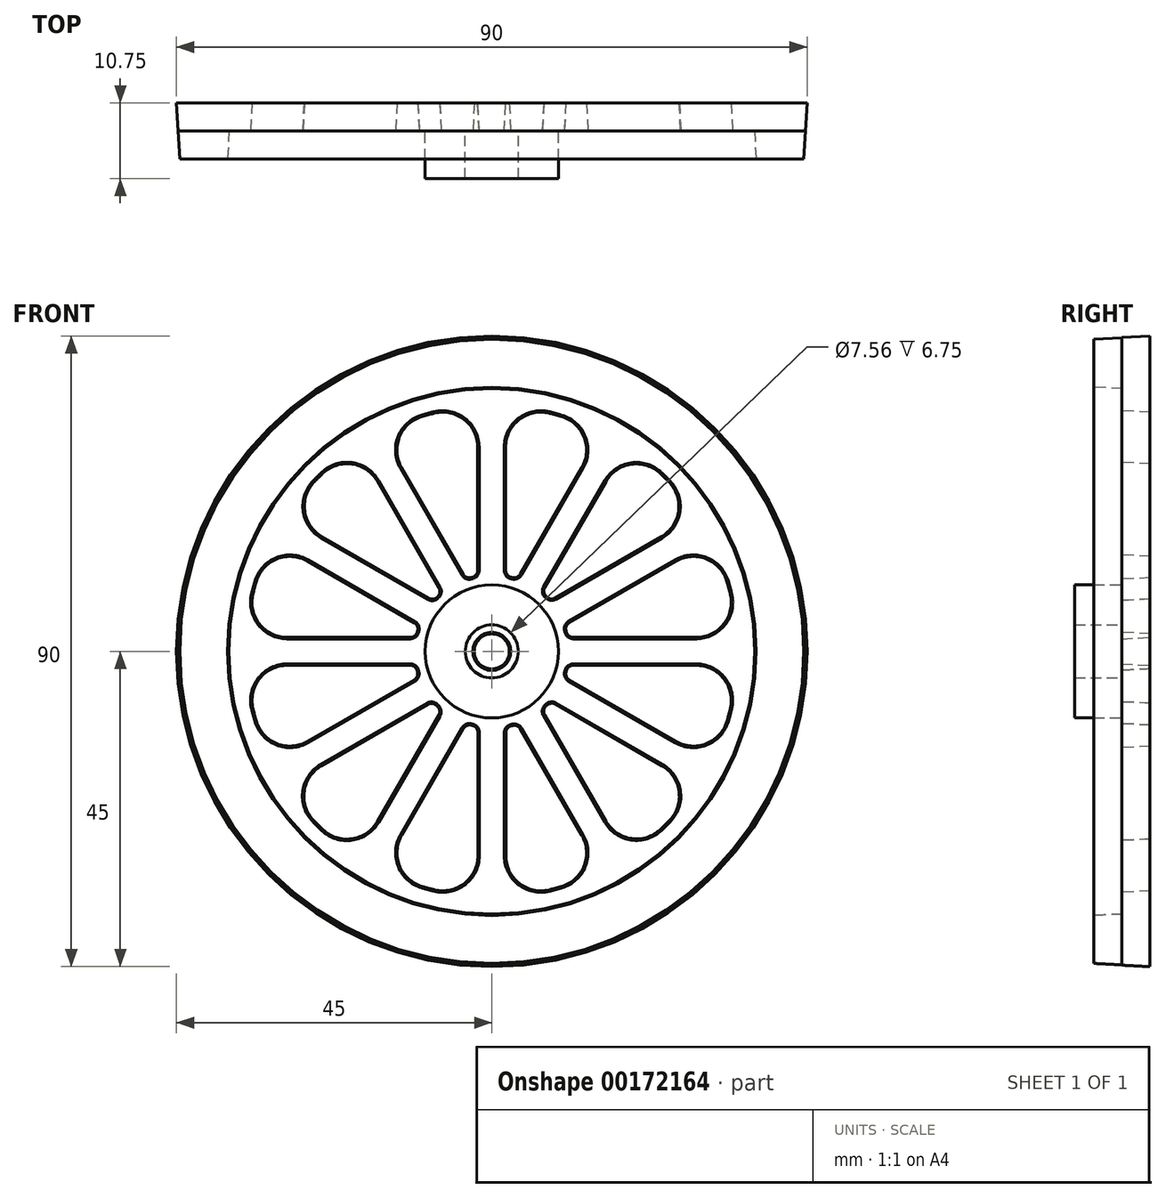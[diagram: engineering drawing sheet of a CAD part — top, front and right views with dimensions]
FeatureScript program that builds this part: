
annotation { "Feature Type Name" : "Feature", "Feature Type Description" : "" }
export const myFeature = defineFeature(function(context is Context, id is Id, definition is map)
    precondition{}
    {
        {
            var Q0;
            Q0=qCreatedBy(makeId("Front.planeOp"),FACE);
            var sketch = newSketch(context, id + "F0", { "sketchPlane" : qUnion([Q0])});
            skCircle(sketch, "E0", {"center": v(0, 0) * mm, "radius": 2.5 * mm});
            skLineSegment(sketch, "E1", {"start": v(1.99, 29.14) * mm, "end": v(1.99, 11.55) * mm});
            skLineSegment(sketch, "E2", {"start": v(-2.01, 11.55) * mm, "end": v(-2.01, 29.14) * mm});
            skLineSegment(sketch, "E3", {"start": v(4.04, 11) * mm, "end": v(12.85, 26.23) * mm});
            skLineSegment(sketch, "E4", {"start": v(7.56, 9.11) * mm, "end": v(16.3, 24.26) * mm});
            skLineSegment(sketch, "E5", {"start": v(9.04, 7.62) * mm, "end": v(24.2, 16.36) * mm});
            skLineSegment(sketch, "E6", {"start": v(11.06, 4.1) * mm, "end": v(26.26, 12.88) * mm});
            skLineSegment(sketch, "E7", {"start": v(11.62, 2) * mm, "end": v(29.18, 2) * mm});
            skLineSegment(sketch, "E8", {"start": v(11.62, -2) * mm, "end": v(29.17, -2) * mm});
            skLineSegment(sketch, "E9", {"start": v(4.07, -11.06) * mm, "end": v(12.85, -26.27) * mm});
            skLineSegment(sketch, "E10", {"start": v(2, -11.62) * mm, "end": v(2, -29.18) * mm});
            skLineSegment(sketch, "E11", {"start": v(-1.99, -11.56) * mm, "end": v(-1.99, -29.17) * mm});
            skLineSegment(sketch, "E12", {"start": v(-4.05, -11.01) * mm, "end": v(-12.85, -26.26) * mm});
            skLineSegment(sketch, "E13", {"start": v(-7.57, -9.1) * mm, "end": v(-16.34, -24.3) * mm});
            skLineSegment(sketch, "E14", {"start": v(-9.12, -7.56) * mm, "end": v(-24.31, -16.33) * mm});
            skLineSegment(sketch, "E15", {"start": v(-11.07, -4.06) * mm, "end": v(-26.3, -12.85) * mm});
            skLineSegment(sketch, "E16", {"start": v(-11.06, 4.08) * mm, "end": v(-26.3, 12.88) * mm});
            skLineSegment(sketch, "E17", {"start": v(-9.01, 7.58) * mm, "end": v(-24.25, 16.38) * mm});
            skLineSegment(sketch, "E18", {"start": v(-7.54, 9.05) * mm, "end": v(-16.34, 24.29) * mm});
            skLineSegment(sketch, "E19", {"start": v(-4.08, 11) * mm, "end": v(-12.87, 26.23) * mm});
            skLineSegment(sketch, "E20", {"start": v(26.27, -12.86) * mm, "end": v(11.07, -4.08) * mm});
            skLineSegment(sketch, "E21", {"start": v(7.54, -9.07) * mm, "end": v(16.31, -24.27) * mm});
            skLineSegment(sketch, "E22", {"start": v(9.06, -7.54) * mm, "end": v(24.27, -16.32) * mm});
            skLineSegment(sketch, "E23", {"start": v(-11.63, -2) * mm, "end": v(-29.21, -2) * mm});
            skLineSegment(sketch, "E24", {"start": v(-11.62, 2) * mm, "end": v(-29.22, 2) * mm});
            skArc(sketch, "E25", {"start": v(25.4, -24.1) * mm, "mid": v(24.75, -24.75) * mm, "end": v(24.09, -25.4) * mm});
            skArc(sketch, "E26", {"start": v(9.94, -33.57) * mm, "mid": v(9.06, -33.81) * mm, "end": v(8.17, -34.04) * mm});
            skArc(sketch, "E27", {"start": v(-8.15, -34.03) * mm, "mid": v(-9.05, -33.8) * mm, "end": v(-9.94, -33.56) * mm});
            skArc(sketch, "E28", {"start": v(-24.11, -25.43) * mm, "mid": v(-24.79, -24.77) * mm, "end": v(-25.45, -24.1) * mm});
            skArc(sketch, "E29", {"start": v(-33.6, -9.94) * mm, "mid": v(-33.85, -9.06) * mm, "end": v(-34.08, -8.17) * mm});
            skArc(sketch, "E30", {"start": v(-34.08, 8.16) * mm, "mid": v(-33.85, 9.07) * mm, "end": v(-33.6, 9.97) * mm});
            skArc(sketch, "E31", {"start": v(33.56, -9.95) * mm, "mid": v(33.81, -9.06) * mm, "end": v(34.04, -8.17) * mm});
            skArc(sketch, "E32", {"start": v(34.04, 8.17) * mm, "mid": v(33.81, 9.07) * mm, "end": v(33.56, 9.97) * mm});
            skArc(sketch, "E33", {"start": v(25.31, 24.15) * mm, "mid": v(24.7, 24.77) * mm, "end": v(24.07, 25.38) * mm});
            skArc(sketch, "E34", {"start": v(9.94, 33.53) * mm, "mid": v(9.05, 33.78) * mm, "end": v(8.15, 34) * mm});
            skArc(sketch, "E35", {"start": v(-8.18, 34) * mm, "mid": v(-9.07, 33.78) * mm, "end": v(-9.96, 33.53) * mm});
            skArc(sketch, "E36", {"start": v(-24.1, 25.42) * mm, "mid": v(-24.75, 24.8) * mm, "end": v(-25.37, 24.16) * mm});
            skCircle(sketch, "E37", {"center": v(0, 0) * mm, "radius": 45 * mm});
            skArc(sketch, "E38", {"start": v(-7.8, 7.74) * mm, "mid": v(-7.75, 7.79) * mm, "end": v(-7.7, 7.84) * mm});
            skArc(sketch, "E39", {"start": v(-2.94, 10.53) * mm, "mid": v(-2.85, 10.56) * mm, "end": v(-2.76, 10.58) * mm});
            skArc(sketch, "E40", {"start": v(2.74, 10.58) * mm, "mid": v(2.82, 10.56) * mm, "end": v(2.91, 10.54) * mm});
            skArc(sketch, "E41", {"start": v(7.71, 7.9) * mm, "mid": v(7.77, 7.85) * mm, "end": v(7.83, 7.8) * mm});
            skArc(sketch, "E42", {"start": v(10.6, 2.96) * mm, "mid": v(10.62, 2.86) * mm, "end": v(10.65, 2.75) * mm});
            skArc(sketch, "E43", {"start": v(10.65, -2.76) * mm, "mid": v(10.63, -2.85) * mm, "end": v(10.6, -2.95) * mm});
            skArc(sketch, "E44", {"start": v(7.85, -7.7) * mm, "mid": v(7.78, -7.78) * mm, "end": v(7.7, -7.85) * mm});
            skArc(sketch, "E45", {"start": v(2.94, -10.6) * mm, "mid": v(2.84, -10.63) * mm, "end": v(2.75, -10.65) * mm});
            skArc(sketch, "E46", {"start": v(-2.74, -10.6) * mm, "mid": v(-2.83, -10.57) * mm, "end": v(-2.92, -10.55) * mm});
            skArc(sketch, "E47", {"start": v(-7.73, -7.9) * mm, "mid": v(-7.82, -7.8) * mm, "end": v(-7.9, -7.72) * mm});
            skArc(sketch, "E48", {"start": v(-10.61, -2.92) * mm, "mid": v(-10.64, -2.83) * mm, "end": v(-10.66, -2.74) * mm});
            skArc(sketch, "E49", {"start": v(-10.65, 2.75) * mm, "mid": v(-10.63, 2.85) * mm, "end": v(-10.6, 2.94) * mm});
            skPoint(sketch, "E50.visualSharp", {"position": v(15.73, 31.23) * mm});
            skArc(sketch, "E50.filletArc", {"start": v(12.85, 26.23) * mm, "mid": v(13.16, 30.59) * mm, "end": v(9.94, 33.53) * mm});
            skArc(sketch, "E51.filletArc", {"start": v(8.15, 34) * mm, "mid": v(3.9, 33.07) * mm, "end": v(1.99, 29.14) * mm});
            skArc(sketch, "E52.filletArc", {"start": v(24.07, 25.38) * mm, "mid": v(19.91, 26.7) * mm, "end": v(16.3, 24.26) * mm});
            skPoint(sketch, "E53.visualSharp", {"position": v(29.2, 19.26) * mm});
            skArc(sketch, "E53.filletArc", {"start": v(24.2, 16.36) * mm, "mid": v(26.64, 19.98) * mm, "end": v(25.31, 24.15) * mm});
            skArc(sketch, "E54.filletArc", {"start": v(33.56, 9.97) * mm, "mid": v(30.61, 13.2) * mm, "end": v(26.26, 12.88) * mm});
            skPoint(sketch, "E55.visualSharp", {"position": v(34.95, 2) * mm});
            skArc(sketch, "E55.filletArc", {"start": v(29.18, 2) * mm, "mid": v(33.1, 3.9) * mm, "end": v(34.04, 8.17) * mm});
            skArc(sketch, "E56.filletArc", {"start": v(34.04, -8.17) * mm, "mid": v(33.1, -3.9) * mm, "end": v(29.17, -2) * mm});
            skPoint(sketch, "E57.visualSharp", {"position": v(31.26, -15.74) * mm});
            skArc(sketch, "E57.filletArc", {"start": v(26.27, -12.86) * mm, "mid": v(30.62, -13.17) * mm, "end": v(33.56, -9.95) * mm});
            skPoint(sketch, "E58.visualSharp", {"position": v(29.26, -19.2) * mm});
            skArc(sketch, "E58.filletArc", {"start": v(25.4, -24.1) * mm, "mid": v(26.71, -19.93) * mm, "end": v(24.27, -16.32) * mm});
            skArc(sketch, "E59.filletArc", {"start": v(16.31, -24.27) * mm, "mid": v(19.93, -26.72) * mm, "end": v(24.09, -25.4) * mm});
            skPoint(sketch, "E60.visualSharp", {"position": v(15.74, -31.27) * mm});
            skArc(sketch, "E60.filletArc", {"start": v(9.94, -33.57) * mm, "mid": v(13.17, -30.62) * mm, "end": v(12.85, -26.27) * mm});
            skArc(sketch, "E61.filletArc", {"start": v(2, -29.18) * mm, "mid": v(3.9, -33.1) * mm, "end": v(8.17, -34.04) * mm});
            skPoint(sketch, "E62.visualSharp", {"position": v(-1.99, -34.94) * mm});
            skArc(sketch, "E62.filletArc", {"start": v(-8.15, -34.03) * mm, "mid": v(-3.9, -33.1) * mm, "end": v(-1.99, -29.17) * mm});
            skArc(sketch, "E63.filletArc", {"start": v(-12.85, -26.26) * mm, "mid": v(-13.17, -30.61) * mm, "end": v(-9.94, -33.56) * mm});
            skPoint(sketch, "E64.visualSharp", {"position": v(-19.23, -29.3) * mm});
            skArc(sketch, "E64.filletArc", {"start": v(-24.11, -25.43) * mm, "mid": v(-19.95, -26.75) * mm, "end": v(-16.34, -24.3) * mm});
            skArc(sketch, "E65.filletArc", {"start": v(-24.31, -16.33) * mm, "mid": v(-26.76, -19.94) * mm, "end": v(-25.45, -24.1) * mm});
            skPoint(sketch, "E66.visualSharp", {"position": v(-31.3, -15.74) * mm});
            skArc(sketch, "E66.filletArc", {"start": v(-33.6, -9.94) * mm, "mid": v(-30.66, -13.17) * mm, "end": v(-26.3, -12.85) * mm});
            skArc(sketch, "E67.filletArc", {"start": v(-29.21, -2) * mm, "mid": v(-33.14, -3.9) * mm, "end": v(-34.08, -8.17) * mm});
            skPoint(sketch, "E68.visualSharp", {"position": v(-35, 2) * mm});
            skArc(sketch, "E68.filletArc", {"start": v(-34.08, 8.16) * mm, "mid": v(-33.15, 3.9) * mm, "end": v(-29.22, 2) * mm});
            skArc(sketch, "E69.filletArc", {"start": v(-26.3, 12.88) * mm, "mid": v(-30.66, 13.2) * mm, "end": v(-33.6, 9.97) * mm});
            skArc(sketch, "E70.filletArc", {"start": v(-25.37, 24.16) * mm, "mid": v(-26.7, 20) * mm, "end": v(-24.25, 16.38) * mm});
            skPoint(sketch, "E71.visualSharp", {"position": v(-19.22, 29.29) * mm});
            skArc(sketch, "E71.filletArc", {"start": v(-16.34, 24.29) * mm, "mid": v(-19.95, 26.74) * mm, "end": v(-24.1, 25.42) * mm});
            skArc(sketch, "E72.filletArc", {"start": v(-9.96, 33.53) * mm, "mid": v(-13.18, 30.59) * mm, "end": v(-12.87, 26.23) * mm});
            skPoint(sketch, "E73.visualSharp", {"position": v(-2.01, 34.92) * mm});
            skArc(sketch, "E73.filletArc", {"start": v(-2.01, 29.14) * mm, "mid": v(-3.92, 33.07) * mm, "end": v(-8.18, 34) * mm});
            skPoint(sketch, "E74.newPointB", {"position": v(8.37, 7.18) * mm});
            skArc(sketch, "E74.filletArc", {"start": v(7.83, 7.8) * mm, "mid": v(8.4, 7.5) * mm, "end": v(9.04, 7.62) * mm});
            skPoint(sketch, "E75.visualSharp", {"position": v(7.16, 8.43) * mm});
            skArc(sketch, "E75.filletArc", {"start": v(7.56, 9.11) * mm, "mid": v(7.43, 8.48) * mm, "end": v(7.71, 7.9) * mm});
            skPoint(sketch, "E76.visualSharp", {"position": v(3.64, 10.3) * mm});
            skArc(sketch, "E76.filletArc", {"start": v(2.91, 10.54) * mm, "mid": v(3.56, 10.58) * mm, "end": v(4.04, 11) * mm});
            skPoint(sketch, "E77.visualSharp", {"position": v(1.99, 10.75) * mm});
            skArc(sketch, "E77.filletArc", {"start": v(1.99, 11.55) * mm, "mid": v(2.2, 10.94) * mm, "end": v(2.74, 10.58) * mm});
            skPoint(sketch, "E78.visualSharp", {"position": v(-2.01, 10.75) * mm});
            skArc(sketch, "E78.filletArc", {"start": v(-2.76, 10.58) * mm, "mid": v(-2.22, 10.94) * mm, "end": v(-2.01, 11.55) * mm});
            skPoint(sketch, "E79.visualSharp", {"position": v(-3.67, 10.3) * mm});
            skArc(sketch, "E79.filletArc", {"start": v(-4.08, 11) * mm, "mid": v(-3.59, 10.57) * mm, "end": v(-2.94, 10.53) * mm});
            skPoint(sketch, "E80.visualSharp", {"position": v(-7.14, 8.36) * mm});
            skArc(sketch, "E80.filletArc", {"start": v(-7.7, 7.84) * mm, "mid": v(-7.41, 8.42) * mm, "end": v(-7.54, 9.05) * mm});
            skPoint(sketch, "E81.visualSharp", {"position": v(-8.32, 7.18) * mm});
            skArc(sketch, "E81.filletArc", {"start": v(-9.01, 7.58) * mm, "mid": v(-8.38, 7.45) * mm, "end": v(-7.8, 7.74) * mm});
            skPoint(sketch, "E82.visualSharp", {"position": v(-10.37, 3.68) * mm});
            skArc(sketch, "E82.filletArc", {"start": v(-10.6, 2.94) * mm, "mid": v(-10.64, 3.59) * mm, "end": v(-11.06, 4.08) * mm});
            skPoint(sketch, "E83.visualSharp", {"position": v(-10.82, 2) * mm});
            skArc(sketch, "E83.filletArc", {"start": v(-11.62, 2) * mm, "mid": v(-11, 2.2) * mm, "end": v(-10.65, 2.75) * mm});
            skArc(sketch, "E84.filletArc", {"start": v(-10.66, -2.74) * mm, "mid": v(-11.02, -2.2) * mm, "end": v(-11.63, -2) * mm});
            skPoint(sketch, "E85.visualSharp", {"position": v(-10.37, -3.66) * mm});
            skArc(sketch, "E85.filletArc", {"start": v(-11.07, -4.06) * mm, "mid": v(-10.65, -3.57) * mm, "end": v(-10.61, -2.92) * mm});
            skPoint(sketch, "E86.visualSharp", {"position": v(-8.42, -7.16) * mm});
            skArc(sketch, "E86.filletArc", {"start": v(-7.9, -7.72) * mm, "mid": v(-8.48, -7.43) * mm, "end": v(-9.12, -7.56) * mm});
            skPoint(sketch, "E87.visualSharp", {"position": v(-7.17, -8.41) * mm});
            skArc(sketch, "E87.filletArc", {"start": v(-7.57, -9.1) * mm, "mid": v(-7.44, -8.47) * mm, "end": v(-7.73, -7.9) * mm});
            skPoint(sketch, "E88.visualSharp", {"position": v(-3.65, -10.32) * mm});
            skArc(sketch, "E88.filletArc", {"start": v(-2.92, -10.55) * mm, "mid": v(-3.56, -10.59) * mm, "end": v(-4.05, -11.01) * mm});
            skPoint(sketch, "E89.visualSharp", {"position": v(-1.99, -10.76) * mm});
            skArc(sketch, "E89.filletArc", {"start": v(-1.99, -11.56) * mm, "mid": v(-2.2, -10.95) * mm, "end": v(-2.74, -10.6) * mm});
            skPoint(sketch, "E90.visualSharp", {"position": v(2, -10.82) * mm});
            skArc(sketch, "E90.filletArc", {"start": v(2.75, -10.65) * mm, "mid": v(2.2, -11) * mm, "end": v(2, -11.62) * mm});
            skPoint(sketch, "E91.visualSharp", {"position": v(3.67, -10.37) * mm});
            skArc(sketch, "E91.filletArc", {"start": v(4.07, -11.06) * mm, "mid": v(3.58, -10.64) * mm, "end": v(2.94, -10.6) * mm});
            skPoint(sketch, "E92.visualSharp", {"position": v(7.14, -8.37) * mm});
            skArc(sketch, "E92.filletArc", {"start": v(7.7, -7.85) * mm, "mid": v(7.41, -8.43) * mm, "end": v(7.54, -9.07) * mm});
            skPoint(sketch, "E93.visualSharp", {"position": v(8.37, -7.14) * mm});
            skArc(sketch, "E93.filletArc", {"start": v(9.06, -7.54) * mm, "mid": v(8.43, -7.42) * mm, "end": v(7.85, -7.7) * mm});
            skArc(sketch, "E94.filletArc", {"start": v(10.6, -2.95) * mm, "mid": v(10.64, -3.6) * mm, "end": v(11.07, -4.08) * mm});
            skPoint(sketch, "E95.visualSharp", {"position": v(10.82, -2) * mm});
            skArc(sketch, "E95.filletArc", {"start": v(11.62, -2) * mm, "mid": v(11, -2.21) * mm, "end": v(10.65, -2.76) * mm});
            skPoint(sketch, "E96.visualSharp", {"position": v(10.36, 3.7) * mm});
            skArc(sketch, "E96.filletArc", {"start": v(11.06, 4.1) * mm, "mid": v(10.63, 3.6) * mm, "end": v(10.6, 2.96) * mm});
            skPoint(sketch, "E97.visualSharp", {"position": v(10.82, 2) * mm});
            skArc(sketch, "E97.filletArc", {"start": v(10.65, 2.75) * mm, "mid": v(11, 2.2) * mm, "end": v(11.62, 2) * mm});
            skSolve(sketch);
        }
        {
            var Q0;
            Q0 = qSketchRegion(id + "F0", true);
            extrude(context, id + "F1", {"entities" : qUnion([Q0]), "depth" : 4 * mm, "hasDraft" : true, "draftAngle" : 3 * degree, "draftPullDirection" : true});
        }
        {
            var Q0;
            Q0=makeQuery(id+"F1.opExtrude","CAP_FACE",FACE,{"disambiguationData":[OSD([sQuery(id+"F0.wireOp",EDGE,"E0"),sQuery(id+"F0.wireOp",EDGE,"E1"),sQuery(id+"F0.wireOp",EDGE,"E2"),sQuery(id+"F0.wireOp",EDGE,"E3"),sQuery(id+"F0.wireOp",EDGE,"E4"),sQuery(id+"F0.wireOp",EDGE,"E5"),sQuery(id+"F0.wireOp",EDGE,"E6"),sQuery(id+"F0.wireOp",EDGE,"E7"),sQuery(id+"F0.wireOp",EDGE,"E8"),sQuery(id+"F0.wireOp",EDGE,"E9"),sQuery(id+"F0.wireOp",EDGE,"E10"),sQuery(id+"F0.wireOp",EDGE,"E11"),sQuery(id+"F0.wireOp",EDGE,"E12"),sQuery(id+"F0.wireOp",EDGE,"E13"),sQuery(id+"F0.wireOp",EDGE,"E14"),sQuery(id+"F0.wireOp",EDGE,"E15"),sQuery(id+"F0.wireOp",EDGE,"E16"),sQuery(id+"F0.wireOp",EDGE,"E17"),sQuery(id+"F0.wireOp",EDGE,"E18"),sQuery(id+"F0.wireOp",EDGE,"E19"),sQuery(id+"F0.wireOp",EDGE,"E20"),sQuery(id+"F0.wireOp",EDGE,"E21"),sQuery(id+"F0.wireOp",EDGE,"E22"),sQuery(id+"F0.wireOp",EDGE,"E23"),sQuery(id+"F0.wireOp",EDGE,"E24"),sQuery(id+"F0.wireOp",EDGE,"E25"),sQuery(id+"F0.wireOp",EDGE,"E26"),sQuery(id+"F0.wireOp",EDGE,"E27"),sQuery(id+"F0.wireOp",EDGE,"E28"),sQuery(id+"F0.wireOp",EDGE,"E29"),sQuery(id+"F0.wireOp",EDGE,"E30"),sQuery(id+"F0.wireOp",EDGE,"E31"),sQuery(id+"F0.wireOp",EDGE,"E32"),sQuery(id+"F0.wireOp",EDGE,"E33"),sQuery(id+"F0.wireOp",EDGE,"E34"),sQuery(id+"F0.wireOp",EDGE,"E35"),sQuery(id+"F0.wireOp",EDGE,"E36"),sQuery(id+"F0.wireOp",EDGE,"E37"),sQuery(id+"F0.wireOp",EDGE,"E38"),sQuery(id+"F0.wireOp",EDGE,"E39"),sQuery(id+"F0.wireOp",EDGE,"E40"),sQuery(id+"F0.wireOp",EDGE,"E41"),sQuery(id+"F0.wireOp",EDGE,"E42"),sQuery(id+"F0.wireOp",EDGE,"E43"),sQuery(id+"F0.wireOp",EDGE,"E44"),sQuery(id+"F0.wireOp",EDGE,"E45"),sQuery(id+"F0.wireOp",EDGE,"E46"),sQuery(id+"F0.wireOp",EDGE,"E47"),sQuery(id+"F0.wireOp",EDGE,"E48"),sQuery(id+"F0.wireOp",EDGE,"E49"),sQuery(id+"F0.wireOp",EDGE,"E50.filletArc"),sQuery(id+"F0.wireOp",EDGE,"E51.filletArc"),sQuery(id+"F0.wireOp",EDGE,"E52.filletArc"),sQuery(id+"F0.wireOp",EDGE,"E53.filletArc"),sQuery(id+"F0.wireOp",EDGE,"E54.filletArc"),sQuery(id+"F0.wireOp",EDGE,"E55.filletArc"),sQuery(id+"F0.wireOp",EDGE,"E56.filletArc"),sQuery(id+"F0.wireOp",EDGE,"E57.filletArc"),sQuery(id+"F0.wireOp",EDGE,"E58.filletArc"),sQuery(id+"F0.wireOp",EDGE,"E59.filletArc"),sQuery(id+"F0.wireOp",EDGE,"E60.filletArc"),sQuery(id+"F0.wireOp",EDGE,"E61.filletArc"),sQuery(id+"F0.wireOp",EDGE,"E62.filletArc"),sQuery(id+"F0.wireOp",EDGE,"E63.filletArc"),sQuery(id+"F0.wireOp",EDGE,"E64.filletArc"),sQuery(id+"F0.wireOp",EDGE,"E65.filletArc"),sQuery(id+"F0.wireOp",EDGE,"E66.filletArc"),sQuery(id+"F0.wireOp",EDGE,"E67.filletArc"),sQuery(id+"F0.wireOp",EDGE,"E68.filletArc"),sQuery(id+"F0.wireOp",EDGE,"E69.filletArc"),sQuery(id+"F0.wireOp",EDGE,"E70.filletArc"),sQuery(id+"F0.wireOp",EDGE,"E71.filletArc"),sQuery(id+"F0.wireOp",EDGE,"E72.filletArc"),sQuery(id+"F0.wireOp",EDGE,"E73.filletArc"),sQuery(id+"F0.wireOp",EDGE,"E74.filletArc"),sQuery(id+"F0.wireOp",EDGE,"E75.filletArc"),sQuery(id+"F0.wireOp",EDGE,"E76.filletArc"),sQuery(id+"F0.wireOp",EDGE,"E77.filletArc"),sQuery(id+"F0.wireOp",EDGE,"E78.filletArc"),sQuery(id+"F0.wireOp",EDGE,"E79.filletArc"),sQuery(id+"F0.wireOp",EDGE,"E80.filletArc"),sQuery(id+"F0.wireOp",EDGE,"E81.filletArc"),sQuery(id+"F0.wireOp",EDGE,"E82.filletArc"),sQuery(id+"F0.wireOp",EDGE,"E83.filletArc"),sQuery(id+"F0.wireOp",EDGE,"E84.filletArc"),sQuery(id+"F0.wireOp",EDGE,"E85.filletArc"),sQuery(id+"F0.wireOp",EDGE,"E86.filletArc"),sQuery(id+"F0.wireOp",EDGE,"E87.filletArc"),sQuery(id+"F0.wireOp",EDGE,"E88.filletArc"),sQuery(id+"F0.wireOp",EDGE,"E89.filletArc"),sQuery(id+"F0.wireOp",EDGE,"E90.filletArc"),sQuery(id+"F0.wireOp",EDGE,"E91.filletArc"),sQuery(id+"F0.wireOp",EDGE,"E92.filletArc"),sQuery(id+"F0.wireOp",EDGE,"E93.filletArc"),sQuery(id+"F0.wireOp",EDGE,"E94.filletArc"),sQuery(id+"F0.wireOp",EDGE,"E95.filletArc"),sQuery(id+"F0.wireOp",EDGE,"E96.filletArc"),sQuery(id+"F0.wireOp",EDGE,"E97.filletArc")])],"isStart":false});
            var sketch = newSketch(context, id + "F2", { "sketchPlane" : qUnion([Q0])});
            skCircle(sketch, "E98", {"center": v(0, 0) * mm, "radius": 44.75 * mm});
            skCircle(sketch, "E99", {"center": v(0, 0) * mm, "radius": 37.5 * mm});
            skCircle(sketch, "E100", {"center": v(0, 0) * mm, "radius": 2.5 * mm});
            skCircle(sketch, "E101", {"center": v(0, 0) * mm, "radius": 3.78 * mm});
            skCircle(sketch, "E102", {"center": v(0, 0) * mm, "radius": 9.5 * mm});
            skSolve(sketch);
        }
        {
            var Q0;
            Q0 = qSketchRegion(id + "F2", true);
            extrude(context, id + "F3", {"entities" : qUnion([Q0]), "operationType" : NewBodyOperationType.ADD, "depth" : 4 * mm, "hasDraft" : true, "draftAngle" : 3 * degree, "draftPullDirection" : true});
        }
        {
            var Q0;
            Q0=makeQuery(id+"F2.imprint","IMPRINT",FACE,{"disambiguationData":[TD([[makeQuery(id+"F2.imprint","IMPRINT",EDGE,{"derivedFrom":sQuery(id+"F2.wireOp",EDGE,"E101")}),-1.0]])]});
            extrude(context, id + "F4", {"entities" : qUnion([Q0]), "operationType" : NewBodyOperationType.ADD, "depth" : 6.75 * mm});
        }
    });
